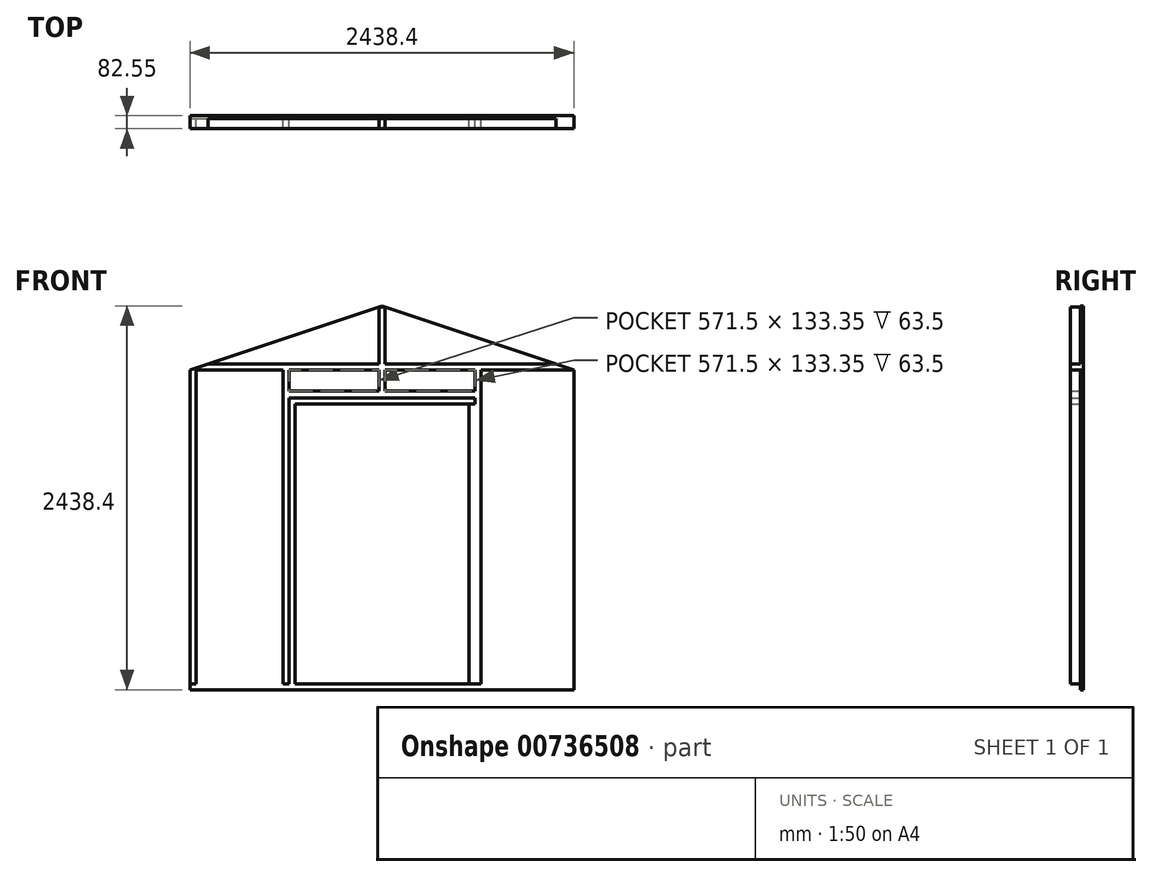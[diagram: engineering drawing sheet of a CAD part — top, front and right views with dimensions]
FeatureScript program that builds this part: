
annotation { "Feature Type Name" : "Feature", "Feature Type Description" : "" }
export const myFeature = defineFeature(function(context is Context, id is Id, definition is map)
    precondition{}
    {
        {
            var Q0;
            Q0=qCreatedBy(makeId("Front.planeOp"),FACE);
            var sketch = newSketch(context, id + "F0", { "sketchPlane" : qUnion([Q0])});
            skLineSegment(sketch, "E0.bottom", {"start": v(1219.2, 1016) * mm, "end": v(-1219.2, 1016) * mm, "construction": true});
            skLineSegment(sketch, "E0.top", {"start": v(1219.2, -1016) * mm, "end": v(-1219.2, -1016) * mm});
            skLineSegment(sketch, "E0.left", {"start": v(1219.2, 1016) * mm, "end": v(1219.2, -1016) * mm});
            skLineSegment(sketch, "E0.right", {"start": v(-1219.2, 1016) * mm, "end": v(-1219.2, -1016) * mm});
            skPoint(sketch, "E0.middle", {"position": v(0, 0) * mm});
            skLineSegment(sketch, "E1", {"start": v(-1219.2, 1016) * mm, "end": v(0, 1422.4) * mm});
            skLineSegment(sketch, "E2", {"start": v(0, 1422.4) * mm, "end": v(1219.2, 1016) * mm});
            skLineSegment(sketch, "E3", {"start": v(-1219.2, 1016) * mm, "end": v(-1113.18, 1016) * mm});
            skLineSegment(sketch, "E4", {"start": v(-1113.18, 1016) * mm, "end": v(-1113.18, -1016) * mm});
            skSolve(sketch);
        }
        {
            var Q0;
            Q0 = qSketchRegion(id + "F0", true);
            extrude(context, id + "F1", {"entities" : qUnion([Q0]), "depth" : 19.05 * mm, "offsetDistance" : 25.4 * mm});
        }
        {
            var Q0;
            Q0=makeQuery(id+"F1.opExtrude","CAP_FACE",FACE,{"disambiguationData":[OSD([sQuery(id+"F0.wireOp",EDGE,"E0.top"),sQuery(id+"F0.wireOp",EDGE,"E0.left"),sQuery(id+"F0.wireOp",EDGE,"E0.right"),sQuery(id+"F0.wireOp",EDGE,"E1"),sQuery(id+"F0.wireOp",EDGE,"E2")])],"isStart":false});
            var sketch = newSketch(context, id + "F2", { "sketchPlane" : qUnion([Q0])});
            skLineSegment(sketch, "E5", {"start": v(-1219.2, 1016) * mm, "end": v(-1181.1, 1016) * mm});
            skLineSegment(sketch, "E6", {"start": v(-1181.1, 1016) * mm, "end": v(-1181.1, -977.9) * mm});
            skLineSegment(sketch, "E7.0", {"start": v(-1219.2, 1016) * mm, "end": v(-1219.2, -1016) * mm});
            skLineSegment(sketch, "E7.1", {"start": v(1219.2, -1016) * mm, "end": v(-1219.2, -1016) * mm});
            skLineSegment(sketch, "E8", {"start": v(-1219.2, 1016) * mm, "end": v(1219.2, 1016) * mm});
            skLineSegment(sketch, "E9", {"start": v(1219.2, 1016) * mm, "end": v(1104.9, 1054.1) * mm});
            skLineSegment(sketch, "E10", {"start": v(1104.9, 1054.1) * mm, "end": v(-1104.9, 1054.1) * mm});
            skLineSegment(sketch, "E11", {"start": v(-1104.9, 1054.1) * mm, "end": v(-1219.2, 1016) * mm});
            skLineSegment(sketch, "E12", {"start": v(1219.2, 1016) * mm, "end": v(1181.1, 1016) * mm});
            skLineSegment(sketch, "E13", {"start": v(1181.1, 1016) * mm, "end": v(1181.1, -977.9) * mm});
            skLineSegment(sketch, "E14", {"start": v(0, 1422.4) * mm, "end": v(0, 1054.1) * mm, "construction": true});
            skLineSegment(sketch, "E15.trimOffspring", {"start": v(0, 1016) * mm, "end": v(0, 882.65) * mm, "construction": true});
            skLineSegment(sketch, "E16", {"start": v(-609.6, 1016) * mm, "end": v(-609.6, -977.9) * mm, "construction": true});
            skLineSegment(sketch, "E17", {"start": v(609.6, 1016) * mm, "end": v(609.6, -977.9) * mm, "construction": true});
            skLineSegment(sketch, "E18", {"start": v(-609.6, -1016) * mm, "end": v(-590.55, -1016) * mm});
            skLineSegment(sketch, "E19", {"start": v(-590.55, -977.9) * mm, "end": v(-590.55, 1016) * mm});
            skLineSegment(sketch, "E20", {"start": v(-628.65, 1016) * mm, "end": v(-628.65, -977.9) * mm});
            skLineSegment(sketch, "E21.MirrorCS", {"start": v(590.55, -977.9) * mm, "end": v(590.55, 1016) * mm});
            skLineSegment(sketch, "E22.MirrorCS", {"start": v(628.65, 1016) * mm, "end": v(628.65, -977.9) * mm});
            skLineSegment(sketch, "E23", {"start": v(-19.05, 1016) * mm, "end": v(-19.05, 882.65) * mm});
            skLineSegment(sketch, "E24", {"start": v(-1219.2, -977.9) * mm, "end": v(1219.2, -977.9) * mm});
            skLineSegment(sketch, "E25", {"start": v(-19.05, 1054.1) * mm, "end": v(-19.05, 1416.05) * mm});
            skLineSegment(sketch, "E26", {"start": v(19.05, 1054.1) * mm, "end": v(19.05, 1416.05) * mm});
            skLineSegment(sketch, "E27", {"start": v(-19.05, 1416.05) * mm, "end": v(19.05, 1416.05) * mm});
            skLineSegment(sketch, "E28", {"start": v(-590.55, -977.9) * mm, "end": v(-590.55, 800.1) * mm});
            skLineSegment(sketch, "E29", {"start": v(-590.55, 800.1) * mm, "end": v(-552.45, 800.1) * mm});
            skLineSegment(sketch, "E30", {"start": v(-552.45, 800.1) * mm, "end": v(-552.45, -977.9) * mm});
            skLineSegment(sketch, "E31", {"start": v(590.55, 800.1) * mm, "end": v(552.45, 800.1) * mm});
            skLineSegment(sketch, "E32", {"start": v(552.45, 800.1) * mm, "end": v(552.45, -977.9) * mm});
            skLineSegment(sketch, "E33", {"start": v(-590.55, 800.1) * mm, "end": v(-590.55, 838.2) * mm});
            skLineSegment(sketch, "E34", {"start": v(-590.55, 838.2) * mm, "end": v(590.55, 838.2) * mm});
            skLineSegment(sketch, "E35", {"start": v(-590.55, 800.1) * mm, "end": v(590.55, 800.1) * mm});
            skLineSegment(sketch, "E36", {"start": v(-590.55, 882.65) * mm, "end": v(590.55, 882.65) * mm});
            skLineSegment(sketch, "E37", {"start": v(-590.55, 844.55) * mm, "end": v(590.55, 844.55) * mm});
            skLineSegment(sketch, "E38.trimOffspring", {"start": v(19.05, 882.65) * mm, "end": v(19.05, 1016) * mm});
            skSolve(sketch);
        }
        {
            var Q0;
            {var subQ0=sQuery(id+"F2.wireOp",EDGE,"E25");Q0=makeQuery(id+"F2.imprint","IMPRINT",FACE,{"disambiguationData":[TD([[makeQuery(id+"F2.imprint","IMPRINT",EDGE,{"derivedFrom":subQ0}),-1.0]])]});}
            var Q1;
            {var subQ1=sQuery(id+"F2.wireOp",EDGE,"E9");Q1=makeQuery(id+"F2.imprint","IMPRINT",FACE,{"disambiguationData":[TD([[makeQuery(id+"F2.imprint","IMPRINT",EDGE,{"derivedFrom":subQ1}),-1.0]])]});}
            var Q2;
            {var subQ0=sQuery(id+"F2.wireOp",EDGE,"E23");Q2=makeQuery(id+"F2.imprint","IMPRINT",FACE,{"disambiguationData":[TD([[makeQuery(id+"F2.imprint","IMPRINT",EDGE,{"derivedFrom":subQ0}),1.0]])]});}
            var Q3;
            {var subQ5=sQuery(id+"F2.wireOp",EDGE,"E20");Q3=makeQuery(id+"F2.imprint","IMPRINT",FACE,{"disambiguationData":[TD([[makeQuery(id+"F2.imprint","IMPRINT",EDGE,{"derivedFrom":subQ5}),1.0]])]});}
            var Q4;
            {var subQ5=sQuery(id+"F2.wireOp",EDGE,"E22.MirrorCS");Q4=makeQuery(id+"F2.imprint","IMPRINT",FACE,{"disambiguationData":[TD([[makeQuery(id+"F2.imprint","IMPRINT",EDGE,{"derivedFrom":subQ5}),-1.0]])]});}
            var Q5;
            {var subQ0=sQuery(id+"F2.wireOp",EDGE,"E12");Q5=makeQuery(id+"F2.imprint","IMPRINT",FACE,{"disambiguationData":[TD([[makeQuery(id+"F2.imprint","IMPRINT",EDGE,{"derivedFrom":subQ0}),1.0]])]});}
            var Q6;
            {var subQ0=sQuery(id+"F2.wireOp",EDGE,"E6");Q6=makeQuery(id+"F2.imprint","IMPRINT",FACE,{"disambiguationData":[TD([[makeQuery(id+"F2.imprint","IMPRINT",EDGE,{"derivedFrom":subQ0}),-1.0]])]});}
            var Q7;
            {var subQ13=sQuery(id+"F2.wireOp",EDGE,"E18");Q7=makeQuery(id+"F2.imprint","IMPRINT",FACE,{"disambiguationData":[TD([[makeQuery(id+"F2.imprint","IMPRINT",EDGE,{"derivedFrom":subQ13}),-1.0]])]});}
            extrude(context, id + "F3", {"entities" : qUnion([Q0, Q1, Q2, Q3, Q4, Q5, Q6, Q7]), "operationType" : NewBodyOperationType.ADD, "depth" : 63.5 * mm, "offsetDistance" : 25.4 * mm});
        }
        {
            var Q0;
            {var subQ0=sQuery(id+"F2.wireOp",EDGE,"E28");Q0=makeQuery(id+"F2.imprint","IMPRINT",FACE,{"disambiguationData":[TD([[makeQuery(id+"F2.imprint","IMPRINT",EDGE,{"derivedFrom":subQ0}),-1.0]])]});}
            var Q1;
            {var subQ5=sQuery(id+"F2.wireOp",EDGE,"E32");Q1=makeQuery(id+"F2.imprint","IMPRINT",FACE,{"disambiguationData":[TD([[makeQuery(id+"F2.imprint","IMPRINT",EDGE,{"derivedFrom":subQ5}),1.0]])]});}
            var Q2;
            {var subQ5=sQuery(id+"F2.wireOp",EDGE,"E37");Q2=makeQuery(id+"F2.imprint","IMPRINT",FACE,{"disambiguationData":[TD([[makeQuery(id+"F2.imprint","IMPRINT",EDGE,{"derivedFrom":subQ5}),1.0]])]});}
            var Q3;
            {var subQ1=sQuery(id+"F2.wireOp",EDGE,"E33");Q3=makeQuery(id+"F2.imprint","IMPRINT",FACE,{"disambiguationData":[TD([[makeQuery(id+"F2.imprint","IMPRINT",EDGE,{"derivedFrom":subQ1}),-1.0]])]});}
            var Q4;
            {var subQ0=sQuery(id+"F2.wireOp",EDGE,"E34");Q4=makeQuery(id+"F2.imprint","IMPRINT",FACE,{"disambiguationData":[TD([[makeQuery(id+"F2.imprint","IMPRINT",EDGE,{"derivedFrom":subQ0}),1.0]])]});}
            extrude(context, id + "F4", {"entities" : qUnion([Q0, Q1, Q2, Q3, Q4]), "operationType" : NewBodyOperationType.ADD, "depth" : 63.5 * mm, "offsetDistance" : 25.4 * mm});
        }
        {
            var Q0;
            {var subQ0=sQuery(id+"F2.wireOp",EDGE,"E30");Q0=makeQuery(id+"F2.imprint","IMPRINT",FACE,{"disambiguationData":[TD([[makeQuery(id+"F2.imprint","IMPRINT",EDGE,{"derivedFrom":subQ0}),1.0]])]});}
            extrude(context, id + "F5", {"entities" : qUnion([Q0]), "operationType" : NewBodyOperationType.REMOVE, "endBound" : BoundingType.UP_TO_NEXT, "oppositeDirection" : true, "depth" : 25.4 * mm, "offsetDistance" : 25.4 * mm});
        }
    });
